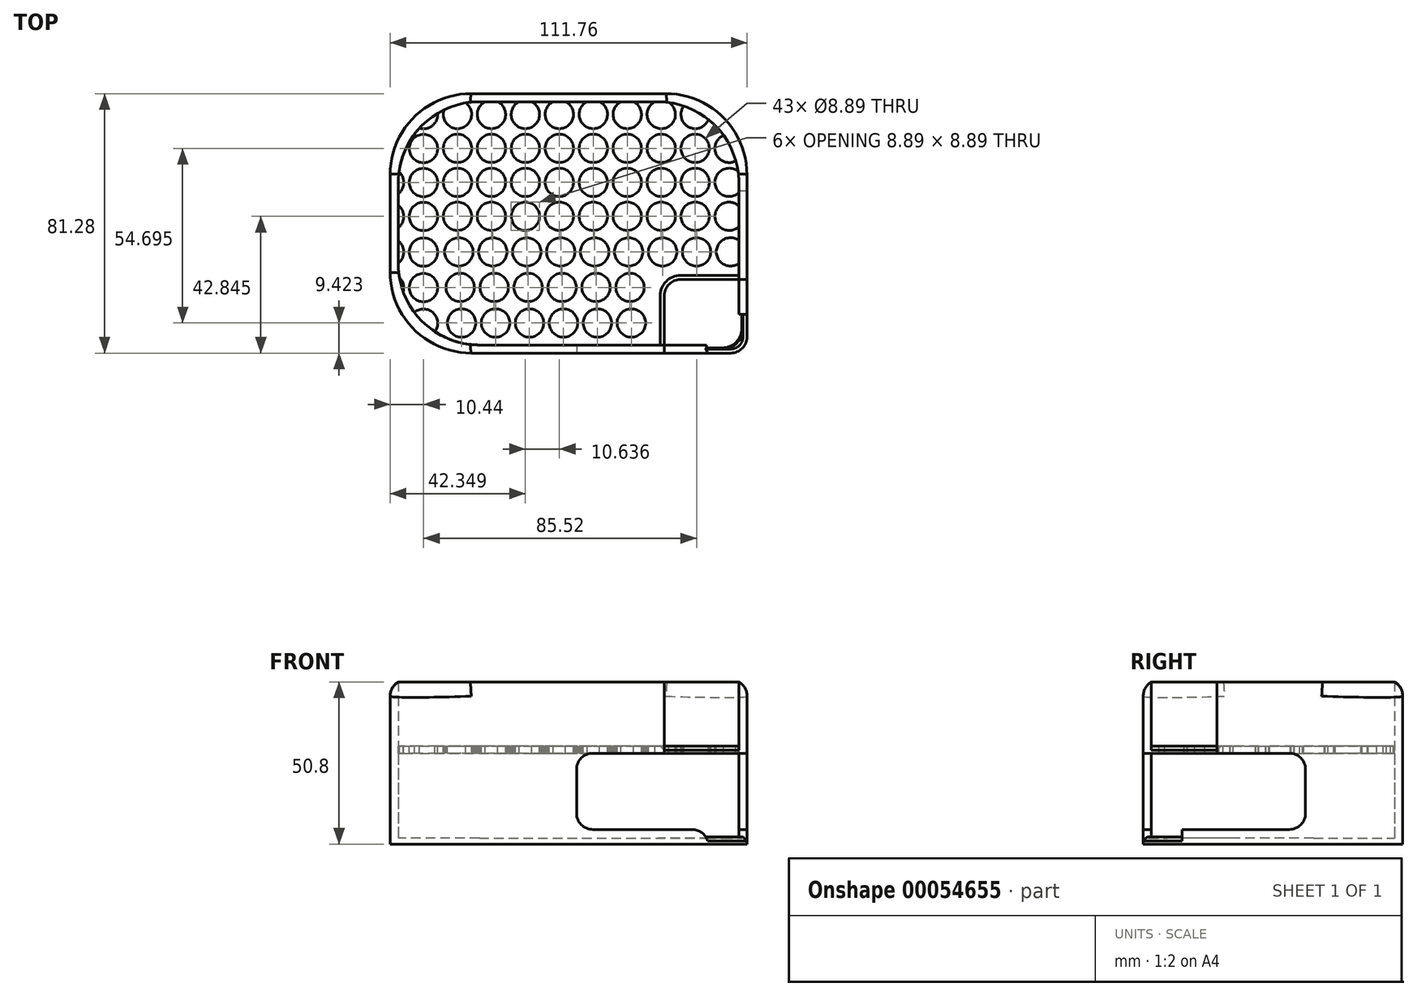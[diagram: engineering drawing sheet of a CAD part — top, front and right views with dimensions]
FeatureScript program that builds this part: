
annotation { "Feature Type Name" : "Feature", "Feature Type Description" : "" }
export const myFeature = defineFeature(function(context is Context, id is Id, definition is map)
    precondition{}
    {
        {
            var Q0;
            Q0=qCreatedBy(makeId("Top.planeOp"),FACE);
            var sketch = newSketch(context, id + "F0", { "sketchPlane" : qUnion([Q0])});
            skLineSegment(sketch, "E0.bottom", {"start": v(-52.81, 43.14) * mm, "end": v(53.87, 43.14) * mm});
            skLineSegment(sketch, "E0.top", {"start": v(-52.81, -33.06) * mm, "end": v(53.87, -33.06) * mm});
            skLineSegment(sketch, "E0.left", {"start": v(-52.81, 43.14) * mm, "end": v(-52.81, -33.06) * mm});
            skLineSegment(sketch, "E0.right", {"start": v(53.87, 43.14) * mm, "end": v(53.87, -33.06) * mm});
            skPoint(sketch, "E0.middle", {"position": v(0.53, 5.04) * mm});
            skLineSegment(sketch, "E1.bottom", {"start": v(56.4, 45.68) * mm, "end": v(-55.35, 45.68) * mm});
            skLineSegment(sketch, "E1.top", {"start": v(56.4, -35.6) * mm, "end": v(-55.35, -35.6) * mm});
            skLineSegment(sketch, "E1.left", {"start": v(56.4, 45.68) * mm, "end": v(56.4, -35.6) * mm});
            skLineSegment(sketch, "E1.right", {"start": v(-55.35, 45.68) * mm, "end": v(-55.35, -35.6) * mm});
            skSolve(sketch);
        }
        {
            var Q0;
            Q0=makeQuery(id+"F0.imprint","IMPRINT",FACE,{"disambiguationData":[TD([[makeQuery(id+"F0.imprint","IMPRINT",EDGE,{"derivedFrom":sQuery(id+"F0.wireOp",EDGE,"E0.bottom")}),-1.0]])]});
            extrude(context, id + "F1", {"entities" : qUnion([Q0]), "depth" : 1.9 * mm});
        }
        {
            var Q0;
            Q0=makeQuery(id+"F0.imprint","IMPRINT",FACE,{"disambiguationData":[TD([[makeQuery(id+"F0.imprint","IMPRINT",EDGE,{"derivedFrom":sQuery(id+"F0.wireOp",EDGE,"E0.bottom")}),1.0]])]});
            extrude(context, id + "F2", {"entities" : qUnion([Q0]), "operationType" : NewBodyOperationType.ADD, "depth" : 50.8 * mm});
        }
        {
            var Q0;
            Q0=makeQuery(id+"F2.opExtrude","SWEPT_FACE",FACE,{"disambiguationData":[OSD([sQuery(id+"F0.wireOp",EDGE,"E0.bottom")])]});
            var sketch = newSketch(context, id + "F3", { "sketchPlane" : qUnion([Q0])});
            skLineSegment(sketch, "E2.bottom", {"start": v(-52.81, 30.73) * mm, "end": v(53.87, 30.73) * mm});
            skLineSegment(sketch, "E2.top", {"start": v(-52.81, 28.45) * mm, "end": v(53.87, 28.45) * mm});
            skLineSegment(sketch, "E2.left", {"start": v(-52.81, 30.73) * mm, "end": v(-52.81, 28.45) * mm});
            skLineSegment(sketch, "E2.right", {"start": v(53.87, 30.73) * mm, "end": v(53.87, 28.45) * mm});
            skSolve(sketch);
        }
        {
            var Q0;
            Q0=makeQuery(id+"F3.imprint","IMPRINT",FACE,{"disambiguationData":[TD([[makeQuery(id+"F3.imprint","IMPRINT",EDGE,{"derivedFrom":sQuery(id+"F3.wireOp",EDGE,"E2.bottom")}),-1.0]])]});
            extrude(context, id + "F4", {"entities" : qUnion([Q0]), "operationType" : NewBodyOperationType.ADD, "depth" : 77.97 * mm});
        }
        {
            var Q0;
            Q0=makeQuery(id+"F2.opExtrude","SWEPT_FACE",FACE,{"disambiguationData":[OSD([sQuery(id+"F0.wireOp",EDGE,"E1.top")])]});
            var sketch = newSketch(context, id + "F5", { "sketchPlane" : qUnion([Q0])});
            skLineSegment(sketch, "E3.bottom", {"start": v(30.51, 50.8) * mm, "end": v(56.4, 50.8) * mm});
            skLineSegment(sketch, "E3.top", {"start": v(30.51, 4.57) * mm, "end": v(56.4, 4.57) * mm});
            skLineSegment(sketch, "E3.left", {"start": v(30.51, 50.8) * mm, "end": v(30.51, 4.57) * mm});
            skLineSegment(sketch, "E3.right", {"start": v(56.4, 50.8) * mm, "end": v(56.4, 4.57) * mm});
            skSolve(sketch);
        }
        {
            var Q0;
            Q0 = qSketchRegion(id + "F5", true);
            extrude(context, id + "F6", {"entities" : qUnion([Q0]), "operationType" : NewBodyOperationType.REMOVE, "oppositeDirection" : true, "depth" : 23.07 * mm});
        }
        {
            var Q0;
            Q0=makeQuery(id+"F2.opExtrude","SWEPT_FACE",FACE,{"disambiguationData":[OSD([sQuery(id+"F0.wireOp",EDGE,"E1.top")])]});
            var sketch = newSketch(context, id + "F7", { "sketchPlane" : qUnion([Q0])});
            skLineSegment(sketch, "E4.bottom", {"start": v(43.46, 4.57) * mm, "end": v(56.4, 4.57) * mm});
            skLineSegment(sketch, "E4.top", {"start": v(43.46, 2.29) * mm, "end": v(56.4, 2.29) * mm});
            skLineSegment(sketch, "E4.left", {"start": v(43.46, 4.57) * mm, "end": v(43.46, 2.29) * mm});
            skLineSegment(sketch, "E4.right", {"start": v(56.4, 4.57) * mm, "end": v(56.4, 2.29) * mm});
            skSolve(sketch);
        }
        {
            var Q0;
            Q0 = qSketchRegion(id + "F7", true);
            extrude(context, id + "F8", {"entities" : qUnion([Q0]), "operationType" : NewBodyOperationType.REMOVE, "oppositeDirection" : true, "depth" : 12.1 * mm});
        }
        {
            var Q0;
            {var subQ0=sQuery(id+"F0.wireOp",EDGE,"E0.bottom");var subQ1=sQuery(id+"F0.wireOp",EDGE,"E0.left");Q0=makeQuery(id+"F4.boolean.opBoolean","SPLIT",EDGE,{"disambiguationData":[TD([makeQuery(id+"F4.opExtrude","SWEPT_FACE",FACE,{"disambiguationData":[OSD([sQuery(id+"F3.wireOp",EDGE,"E2.bottom")])]})])],"derivedFrom":makeQuery(id+"F2.opExtrude","SWEPT_EDGE",EDGE,{"disambiguationData":[OSD([subQ0,subQ1])]})});}
            var Q1;
            {var subQ0=sQuery(id+"F0.wireOp",EDGE,"E0.left");var subQ1=sQuery(id+"F0.wireOp",EDGE,"E0.top");Q1=makeQuery(id+"F4.boolean.opBoolean","SPLIT",EDGE,{"disambiguationData":[TD([makeQuery(id+"F4.opExtrude","SWEPT_FACE",FACE,{"disambiguationData":[OSD([sQuery(id+"F3.wireOp",EDGE,"E2.bottom")])]})])],"derivedFrom":makeQuery(id+"F2.opExtrude","SWEPT_EDGE",EDGE,{"disambiguationData":[OSD([subQ1,subQ0])]})});}
            var Q2;
            {var subQ0=sQuery(id+"F0.wireOp",EDGE,"E0.left");var subQ1=sQuery(id+"F0.wireOp",EDGE,"E0.bottom");Q2=makeQuery(id+"F4.boolean.opBoolean","SPLIT",EDGE,{"disambiguationData":[TD([makeQuery(id+"F4.opExtrude","SWEPT_FACE",FACE,{"disambiguationData":[OSD([sQuery(id+"F3.wireOp",EDGE,"E2.top")])]})])],"derivedFrom":makeQuery(id+"F2.opExtrude","SWEPT_EDGE",EDGE,{"disambiguationData":[OSD([subQ1,subQ0])]})});}
            var Q3;
            {var subQ0=sQuery(id+"F0.wireOp",EDGE,"E0.right");var subQ1=sQuery(id+"F0.wireOp",EDGE,"E0.bottom");Q3=makeQuery(id+"F4.boolean.opBoolean","SPLIT",EDGE,{"disambiguationData":[TD([makeQuery(id+"F4.opExtrude","SWEPT_FACE",FACE,{"disambiguationData":[OSD([sQuery(id+"F3.wireOp",EDGE,"E2.top")])]})])],"derivedFrom":makeQuery(id+"F2.opExtrude","SWEPT_EDGE",EDGE,{"disambiguationData":[OSD([subQ1,subQ0])]})});}
            var Q4;
            {var subQ0=sQuery(id+"F0.wireOp",EDGE,"E0.left");var subQ1=sQuery(id+"F0.wireOp",EDGE,"E0.top");Q4=makeQuery(id+"F4.boolean.opBoolean","SPLIT",EDGE,{"disambiguationData":[TD([makeQuery(id+"F4.opExtrude","SWEPT_FACE",FACE,{"disambiguationData":[OSD([sQuery(id+"F3.wireOp",EDGE,"E2.top")])]})])],"derivedFrom":makeQuery(id+"F2.opExtrude","SWEPT_EDGE",EDGE,{"disambiguationData":[OSD([subQ1,subQ0])]})});}
            var Q5;
            {var subQ0=sQuery(id+"F0.wireOp",EDGE,"E0.bottom");var subQ1=sQuery(id+"F0.wireOp",EDGE,"E0.right");Q5=makeQuery(id+"F4.boolean.opBoolean","SPLIT",EDGE,{"disambiguationData":[TD([makeQuery(id+"F4.opExtrude","SWEPT_FACE",FACE,{"disambiguationData":[OSD([sQuery(id+"F3.wireOp",EDGE,"E2.bottom")])]})])],"derivedFrom":makeQuery(id+"F2.opExtrude","SWEPT_EDGE",EDGE,{"disambiguationData":[OSD([subQ0,subQ1])]})});}
            var Q6;
            Q6=makeQuery(id+"F2.opExtrude","SWEPT_EDGE",EDGE,{"disambiguationData":[OSD([sQuery(id+"F0.wireOp",EDGE,"E1.bottom"),sQuery(id+"F0.wireOp",EDGE,"E1.left")])]});
            var Q7;
            Q7=makeQuery(id+"F2.opExtrude","SWEPT_EDGE",EDGE,{"disambiguationData":[OSD([sQuery(id+"F0.wireOp",EDGE,"E1.bottom"),sQuery(id+"F0.wireOp",EDGE,"E1.right")])]});
            var Q8;
            Q8=makeQuery(id+"F2.opExtrude","SWEPT_EDGE",EDGE,{"disambiguationData":[OSD([sQuery(id+"F0.wireOp",EDGE,"E1.top"),sQuery(id+"F0.wireOp",EDGE,"E1.right")])]});
            fillet(context, id + "F9", {"entities" : qUnion([Q0, Q1, Q2, Q3, Q4, Q5, Q6, Q7, Q8]), "radius" : 25.4 * mm, "tangentPropagation" : true, "allowEdgeOverflow" : false});
        }
        {
            var Q0;
            Q0=makeQuery(id+"F6.boolean.opBoolean","COPY",FACE,{"derivedFrom":makeQuery(id+"F6.opExtrude","SWEPT_FACE",FACE,{"disambiguationData":[OSD([sQuery(id+"F5.wireOp",EDGE,"E3.left")])]})});
            var sketch = newSketch(context, id + "F10", { "sketchPlane" : qUnion([Q0])});
            skLineSegment(sketch, "E5.bottom", {"start": v(-33.06, 28.45) * mm, "end": v(-35.6, 28.45) * mm});
            skLineSegment(sketch, "E5.top", {"start": v(-33.06, 4.57) * mm, "end": v(-35.6, 4.57) * mm});
            skLineSegment(sketch, "E5.left", {"start": v(-33.06, 28.45) * mm, "end": v(-33.06, 4.57) * mm});
            skLineSegment(sketch, "E5.right", {"start": v(-35.6, 28.45) * mm, "end": v(-35.6, 4.57) * mm});
            skSolve(sketch);
        }
        {
            var Q0;
            Q0 = qSketchRegion(id + "F10", true);
            extrude(context, id + "F11", {"entities" : qUnion([Q0]), "operationType" : NewBodyOperationType.REMOVE, "oppositeDirection" : true, "depth" : 27.48 * mm});
        }
        {
            var Q0;
            Q0=makeQuery(id+"F6.boolean.opBoolean","COPY",FACE,{"derivedFrom":makeQuery(id+"F6.opExtrude","CAP_FACE",FACE,{"disambiguationData":[OSD([sQuery(id+"F5.wireOp",EDGE,"E3.bottom"),sQuery(id+"F5.wireOp",EDGE,"E3.top"),sQuery(id+"F5.wireOp",EDGE,"E3.left"),sQuery(id+"F5.wireOp",EDGE,"E3.right")])],"isStart":false})});
            var sketch = newSketch(context, id + "F12", { "sketchPlane" : qUnion([Q0])});
            skLineSegment(sketch, "E6.bottom", {"start": v(53.87, 28.45) * mm, "end": v(56.4, 28.45) * mm});
            skLineSegment(sketch, "E6.top", {"start": v(53.87, 4.57) * mm, "end": v(56.4, 4.57) * mm});
            skLineSegment(sketch, "E6.left", {"start": v(53.87, 28.45) * mm, "end": v(53.87, 4.57) * mm});
            skLineSegment(sketch, "E6.right", {"start": v(56.4, 28.45) * mm, "end": v(56.4, 4.57) * mm});
            skSolve(sketch);
        }
        {
            var Q0;
            Q0 = qSketchRegion(id + "F12", true);
            extrude(context, id + "F13", {"entities" : qUnion([Q0]), "operationType" : NewBodyOperationType.REMOVE, "oppositeDirection" : true, "depth" : 27.75 * mm});
        }
        {
            var Q0;
            Q0=makeQuery(id+"F6.boolean.opBoolean","COPY",EDGE,{"derivedFrom":makeQuery(id+"F6.opExtrude","CAP_EDGE",EDGE,{"disambiguationData":[OSD([sQuery(id+"F5.wireOp",EDGE,"E3.left")])],"isStart":false})});
            var Q1;
            Q1=makeQuery(id+"F13.boolean.opBoolean","COPY",EDGE,{"derivedFrom":makeQuery(id+"F13.opExtrude","CAP_EDGE",EDGE,{"disambiguationData":[OSD([sQuery(id+"F12.wireOp",EDGE,"E6.bottom")])],"isStart":false})});
            var Q2;
            Q2=makeQuery(id+"F13.boolean.opBoolean","COPY",EDGE,{"derivedFrom":makeQuery(id+"F13.opExtrude","CAP_EDGE",EDGE,{"disambiguationData":[OSD([sQuery(id+"F12.wireOp",EDGE,"E6.top")])],"isStart":false})});
            var Q3;
            Q3=makeQuery(id+"F8.boolean.opBoolean","COPY",EDGE,{"derivedFrom":makeQuery(id+"F8.opExtrude","CAP_EDGE",EDGE,{"disambiguationData":[OSD([sQuery(id+"F7.wireOp",EDGE,"E4.bottom")])],"isStart":false})});
            var Q4;
            Q4=makeQuery(id+"F8.boolean.opBoolean","COPY",EDGE,{"derivedFrom":makeQuery(id+"F8.opExtrude","SWEPT_EDGE",EDGE,{"disambiguationData":[OSD([sQuery(id+"F5.wireOp",EDGE,"E3.top"),sQuery(id+"F7.wireOp",EDGE,"E4.bottom"),sQuery(id+"F7.wireOp",EDGE,"E4.left")])]})});
            var Q5;
            Q5=makeQuery(id+"F2.opExtrude","SWEPT_EDGE",EDGE,{"disambiguationData":[OSD([sQuery(id+"F0.wireOp",EDGE,"E1.top"),sQuery(id+"F0.wireOp",EDGE,"E1.left")])]});
            var Q6;
            Q6=makeQuery(id+"F11.boolean.opBoolean","COPY",EDGE,{"derivedFrom":makeQuery(id+"F11.opExtrude","CAP_EDGE",EDGE,{"disambiguationData":[OSD([sQuery(id+"F10.wireOp",EDGE,"E5.top")])],"isStart":false})});
            var Q7;
            Q7=makeQuery(id+"F11.boolean.opBoolean","COPY",EDGE,{"derivedFrom":makeQuery(id+"F11.opExtrude","CAP_EDGE",EDGE,{"disambiguationData":[OSD([sQuery(id+"F10.wireOp",EDGE,"E5.bottom")])],"isStart":false})});
            var Q8;
            Q8=makeQuery(id+"F6.boolean.opBoolean","COPY",EDGE,{"derivedFrom":makeQuery(id+"F6.opExtrude","CAP_EDGE",EDGE,{"disambiguationData":[OSD([sQuery(id+"F5.wireOp",EDGE,"E3.left")])],"isStart":true})});
            var Q9;
            Q9=makeQuery(id+"F6.boolean.opBoolean","COPY",EDGE,{"derivedFrom":makeQuery(id+"F6.opExtrude","CAP_EDGE",EDGE,{"disambiguationData":[OSD([sQuery(id+"F5.wireOp",EDGE,"E3.right")])],"isStart":false})});
            var Q10;
            Q10=makeQuery(id+"F2.opExtrude","CAP_EDGE",EDGE,{"disambiguationData":[OSD([sQuery(id+"F0.wireOp",EDGE,"E1.left")])],"isStart":false});
            fillet(context, id + "F14", {"entities" : qUnion([Q0, Q1, Q2, Q3, Q4, Q5, Q6, Q7, Q8, Q9, Q10]), "radius" : 5.08 * mm, "tangentPropagation" : true, "allowEdgeOverflow" : false});
        }
        {
            var Q0;
            {var subQ0=sQuery(id+"F0.wireOp",EDGE,"E0.right");var subQ1=sQuery(id+"F0.wireOp",EDGE,"E0.top");Q0=makeQuery(id+"F4.boolean.opBoolean","SPLIT",EDGE,{"disambiguationData":[TD([makeQuery(id+"F4.opExtrude","SWEPT_FACE",FACE,{"disambiguationData":[OSD([sQuery(id+"F3.wireOp",EDGE,"E2.top")])]})])],"derivedFrom":makeQuery(id+"F2.opExtrude","SWEPT_EDGE",EDGE,{"disambiguationData":[OSD([subQ1,subQ0])]})});}
            fillet(context, id + "F15", {"entities" : qUnion([Q0]), "radius" : 5.08 * mm, "tangentPropagation" : true, "allowEdgeOverflow" : false});
        }
        {
            var Q0;
            Q0=makeQuery(id+"F14.opFillet","BLEND_EDGE",EDGE,{"blendedFrom":[makeQuery(id+"F2.opExtrude","SWEPT_EDGE",EDGE,{"disambiguationData":[OSD([sQuery(id+"F0.wireOp",EDGE,"E1.top"),sQuery(id+"F0.wireOp",EDGE,"E1.left")])]}),makeQuery(id+"F8.boolean.opBoolean","COPY",FACE,{"derivedFrom":makeQuery(id+"F8.opExtrude","SWEPT_FACE",FACE,{"disambiguationData":[OSD([sQuery(id+"F7.wireOp",EDGE,"E4.top")])]})})],"blendedInto":[makeQuery(id+"F8.boolean.opBoolean","COPY",FACE,{"derivedFrom":makeQuery(id+"F8.opExtrude","SWEPT_FACE",FACE,{"disambiguationData":[OSD([sQuery(id+"F7.wireOp",EDGE,"E4.top")])]})})]});
            var Q1;
            {var subQ0=sQuery(id+"F0.wireOp",EDGE,"E0.right");var subQ1=sQuery(id+"F0.wireOp",EDGE,"E0.top");Q1=makeQuery(id+"F15.opFillet","BLEND_EDGE",EDGE,{"blendedFrom":[makeQuery(id+"F4.boolean.opBoolean","SPLIT",EDGE,{"disambiguationData":[TD([makeQuery(id+"F4.opExtrude","SWEPT_FACE",FACE,{"disambiguationData":[OSD([sQuery(id+"F3.wireOp",EDGE,"E2.top")])]})])],"derivedFrom":makeQuery(id+"F2.opExtrude","SWEPT_EDGE",EDGE,{"disambiguationData":[OSD([subQ1,subQ0])]})}),makeQuery(id+"F8.boolean.opBoolean","COPY",FACE,{"derivedFrom":makeQuery(id+"F8.opExtrude","SWEPT_FACE",FACE,{"disambiguationData":[OSD([sQuery(id+"F7.wireOp",EDGE,"E4.top")])]})})],"blendedInto":[makeQuery(id+"F8.boolean.opBoolean","COPY",FACE,{"derivedFrom":makeQuery(id+"F8.opExtrude","SWEPT_FACE",FACE,{"disambiguationData":[OSD([sQuery(id+"F7.wireOp",EDGE,"E4.top")])]})})]});}
            var Q2;
            Q2=makeQuery(id+"F14.opFillet","BLEND_EDGE",EDGE,{"blendedFrom":[makeQuery(id+"F6.boolean.opBoolean","COPY",EDGE,{"derivedFrom":makeQuery(id+"F6.opExtrude","CAP_EDGE",EDGE,{"disambiguationData":[OSD([sQuery(id+"F5.wireOp",EDGE,"E3.left")])],"isStart":false})}),makeQuery(id+"F4.opExtrude","SWEPT_FACE",FACE,{"disambiguationData":[OSD([sQuery(id+"F3.wireOp",EDGE,"E2.bottom")])]})],"blendedInto":[makeQuery(id+"F4.opExtrude","SWEPT_FACE",FACE,{"disambiguationData":[OSD([sQuery(id+"F3.wireOp",EDGE,"E2.bottom")])]})]});
            var Q3;
            Q3=makeQuery(id+"F11.boolean.opBoolean","COPY",EDGE,{"derivedFrom":makeQuery(id+"F11.opExtrude","CAP_EDGE",EDGE,{"disambiguationData":[OSD([sQuery(id+"F10.wireOp",EDGE,"E5.right")])],"isStart":false})});
            chamfer(context, id + "F16", {"entities" : qUnion([Q0, Q1, Q2, Q3]), "width" : 1.27 * mm, "tangentPropagation" : true});
        }
        {
            var Q0;
            Q0=makeQuery(id+"F4.opExtrude","SWEPT_FACE",FACE,{"disambiguationData":[OSD([sQuery(id+"F3.wireOp",EDGE,"E2.bottom")])]});
            var sketch = newSketch(context, id + "F17", { "sketchPlane" : qUnion([Q0])});
            skCircle(sketch, "E7", {"center": v(-34.27, 7.25) * mm, "radius": 4.44 * mm});
            skCircle(sketch, "E8.0.1.0", {"center": v(-34.27, 17.88) * mm, "radius": 4.44 * mm});
            skCircle(sketch, "E8.0.2.0", {"center": v(-34.27, 28.52) * mm, "radius": 4.44 * mm});
            skArc(sketch, "E8.0.3.0", {"start": v(-38.47, 40.61) * mm, "mid": v(-32.92, 34.92) * mm, "end": v(-31.7, 42.78) * mm});
            skCircle(sketch, "E8.1.0.0", {"center": v(-23.64, 7.25) * mm, "radius": 4.44 * mm});
            skCircle(sketch, "E8.1.1.0", {"center": v(-23.64, 17.88) * mm, "radius": 4.44 * mm});
            skCircle(sketch, "E8.1.2.0", {"center": v(-23.64, 28.52) * mm, "radius": 4.44 * mm});
            skArc(sketch, "E8.1.3.0", {"start": v(-25.6, 43.14) * mm, "mid": v(-23.64, 34.71) * mm, "end": v(-21.68, 43.14) * mm});
            skCircle(sketch, "E8.2.0.0", {"center": v(-13, 7.25) * mm, "radius": 4.44 * mm});
            skCircle(sketch, "E8.2.1.0", {"center": v(-13, 17.88) * mm, "radius": 4.44 * mm});
            skCircle(sketch, "E8.2.2.0", {"center": v(-13, 28.52) * mm, "radius": 4.44 * mm});
            skArc(sketch, "E8.2.3.0", {"start": v(-14.96, 43.14) * mm, "mid": v(-13, 34.71) * mm, "end": v(-11.05, 43.14) * mm});
            skCircle(sketch, "E8.3.0.0", {"center": v(-2.37, 7.25) * mm, "radius": 4.44 * mm});
            skCircle(sketch, "E8.3.1.0", {"center": v(-2.37, 17.88) * mm, "radius": 4.44 * mm});
            skCircle(sketch, "E8.3.2.0", {"center": v(-2.37, 28.52) * mm, "radius": 4.44 * mm});
            skArc(sketch, "E8.3.3.0", {"start": v(-4.32, 43.14) * mm, "mid": v(-2.37, 34.71) * mm, "end": v(-0.4, 43.14) * mm});
            skCircle(sketch, "E8.4.0.0", {"center": v(8.27, 7.25) * mm, "radius": 4.44 * mm});
            skCircle(sketch, "E8.4.1.0", {"center": v(8.27, 17.88) * mm, "radius": 4.44 * mm});
            skCircle(sketch, "E8.4.2.0", {"center": v(8.27, 28.52) * mm, "radius": 4.44 * mm});
            skArc(sketch, "E8.4.3.0", {"start": v(6.32, 43.14) * mm, "mid": v(8.27, 34.71) * mm, "end": v(10.23, 43.14) * mm});
            skCircle(sketch, "E8.5.0.0", {"center": v(18.9, 7.25) * mm, "radius": 4.44 * mm});
            skCircle(sketch, "E8.5.1.0", {"center": v(18.9, 17.88) * mm, "radius": 4.44 * mm});
            skCircle(sketch, "E8.5.2.0", {"center": v(18.9, 28.52) * mm, "radius": 4.44 * mm});
            skArc(sketch, "E8.5.3.0", {"start": v(16.95, 43.14) * mm, "mid": v(18.9, 34.71) * mm, "end": v(20.86, 43.14) * mm});
            skCircle(sketch, "E8.6.0.0", {"center": v(29.54, 7.25) * mm, "radius": 4.44 * mm});
            skCircle(sketch, "E8.6.1.0", {"center": v(29.54, 17.88) * mm, "radius": 4.44 * mm});
            skCircle(sketch, "E8.6.2.0", {"center": v(29.54, 28.52) * mm, "radius": 4.44 * mm});
            skArc(sketch, "E8.6.3.0", {"start": v(27.59, 43.14) * mm, "mid": v(29.3, 34.72) * mm, "end": v(31.92, 42.9) * mm});
            skCircle(sketch, "E8.7.0.0", {"center": v(40.18, 7.25) * mm, "radius": 4.44 * mm});
            skCircle(sketch, "E8.7.1.0", {"center": v(40.18, 17.88) * mm, "radius": 4.44 * mm});
            skCircle(sketch, "E8.7.2.0", {"center": v(40.18, 28.52) * mm, "radius": 4.44 * mm});
            skArc(sketch, "E8.7.3.0", {"start": v(36.61, 41.8) * mm, "mid": v(38.05, 35.26) * mm, "end": v(44.33, 37.58) * mm});
            skArc(sketch, "E8.8.0.0", {"start": v(53.87, 10.48) * mm, "mid": v(46.37, 7.25) * mm, "end": v(53.87, 4.01) * mm});
            skArc(sketch, "E8.8.1.0", {"start": v(53.6, 21.34) * mm, "mid": v(46.38, 17.71) * mm, "end": v(53.87, 14.65) * mm});
            skArc(sketch, "E8.8.2.0", {"start": v(49.07, 32.6) * mm, "mid": v(46.81, 26.59) * mm, "end": v(52.92, 24.6) * mm});
            skLineSegment(sketch, "E8.direction1", {"start": v(-34.27, 7.25) * mm, "end": v(-23.64, 7.25) * mm, "construction": true});
            skLineSegment(sketch, "E8.direction2", {"start": v(-34.27, 7.25) * mm, "end": v(-34.27, 17.88) * mm, "construction": true});
            skPoint(sketch, "E9", {"position": v(-38.47, 40.61) * mm});
            skPoint(sketch, "E10", {"position": v(-31.7, 42.78) * mm});
            skPoint(sketch, "E11", {"position": v(-21.68, 43.14) * mm});
            skPoint(sketch, "E12", {"position": v(-11.05, 43.14) * mm});
            skPoint(sketch, "E13", {"position": v(-14.96, 43.14) * mm});
            skPoint(sketch, "E14", {"position": v(-4.32, 43.14) * mm});
            skPoint(sketch, "E15", {"position": v(-0.4, 43.14) * mm});
            skPoint(sketch, "E16", {"position": v(16.95, 43.14) * mm});
            skPoint(sketch, "E17", {"position": v(20.86, 43.14) * mm});
            skPoint(sketch, "E18", {"position": v(10.23, 43.14) * mm});
            skPoint(sketch, "E19", {"position": v(6.32, 43.14) * mm});
            skPoint(sketch, "E20", {"position": v(-25.6, 43.14) * mm});
            skPoint(sketch, "E21", {"position": v(27.59, 43.14) * mm});
            skPoint(sketch, "E22", {"position": v(31.92, 42.9) * mm});
            skPoint(sketch, "E23", {"position": v(36.61, 41.8) * mm});
            skPoint(sketch, "E24", {"position": v(44.33, 37.58) * mm});
            skPoint(sketch, "E25", {"position": v(49.07, 32.6) * mm});
            skPoint(sketch, "E26", {"position": v(52.92, 24.6) * mm});
            skPoint(sketch, "E27", {"position": v(53.6, 21.34) * mm});
            skPoint(sketch, "E28", {"position": v(53.87, 14.65) * mm});
            skPoint(sketch, "E29", {"position": v(53.87, 10.48) * mm});
            skPoint(sketch, "E30", {"position": v(53.87, 4.01) * mm});
            skCircle(sketch, "E31.0.1.0", {"center": v(-33.84, -3.9) * mm, "radius": 4.44 * mm});
            skCircle(sketch, "E31.0.2.0", {"center": v(-33.41, -15.04) * mm, "radius": 4.44 * mm});
            skCircle(sketch, "E31.0.3.0", {"center": v(-32.99, -26.18) * mm, "radius": 4.44 * mm});
            skCircle(sketch, "E31.1.1.0", {"center": v(-23.2, -3.9) * mm, "radius": 4.44 * mm});
            skCircle(sketch, "E31.1.2.0", {"center": v(-22.78, -15.04) * mm, "radius": 4.44 * mm});
            skCircle(sketch, "E31.1.3.0", {"center": v(-22.35, -26.18) * mm, "radius": 4.44 * mm});
            skCircle(sketch, "E31.2.1.0", {"center": v(-12.57, -3.9) * mm, "radius": 4.44 * mm});
            skCircle(sketch, "E31.2.2.0", {"center": v(-12.14, -15.04) * mm, "radius": 4.44 * mm});
            skCircle(sketch, "E31.2.3.0", {"center": v(-11.71, -26.18) * mm, "radius": 4.44 * mm});
            skCircle(sketch, "E31.3.1.0", {"center": v(-1.94, -3.9) * mm, "radius": 4.44 * mm});
            skCircle(sketch, "E31.3.2.0", {"center": v(-1.5, -15.04) * mm, "radius": 4.44 * mm});
            skCircle(sketch, "E31.3.3.0", {"center": v(-1.08, -26.18) * mm, "radius": 4.44 * mm});
            skCircle(sketch, "E31.4.1.0", {"center": v(8.7, -3.9) * mm, "radius": 4.44 * mm});
            skCircle(sketch, "E31.4.2.0", {"center": v(9.13, -15.04) * mm, "radius": 4.44 * mm});
            skCircle(sketch, "E31.4.3.0", {"center": v(9.56, -26.18) * mm, "radius": 4.44 * mm});
            skCircle(sketch, "E31.5.1.0", {"center": v(19.34, -3.9) * mm, "radius": 4.44 * mm});
            skCircle(sketch, "E31.5.2.0", {"center": v(19.77, -15.04) * mm, "radius": 4.44 * mm});
            skCircle(sketch, "E31.5.3.0", {"center": v(20.2, -26.18) * mm, "radius": 4.44 * mm});
            skCircle(sketch, "E31.6.1.0", {"center": v(29.97, -3.9) * mm, "radius": 4.44 * mm});
            skCircle(sketch, "E31.7.1.0", {"center": v(40.6, -3.9) * mm, "radius": 4.44 * mm});
            skArc(sketch, "E31.8.0.0", {"start": v(50.82, 11.69) * mm, "mid": v(46.37, 7.25) * mm, "end": v(50.82, 2.8) * mm});
            skArc(sketch, "E31.8.1.0", {"start": v(53.87, -0.3) * mm, "mid": v(46.8, -3.9) * mm, "end": v(53.87, -7.48) * mm});
            skLineSegment(sketch, "E31.direction2", {"start": v(-34.27, 7.25) * mm, "end": v(-33.84, -3.9) * mm, "construction": true});
            skPoint(sketch, "E32", {"position": v(53.87, -0.3) * mm});
            skPoint(sketch, "E33", {"position": v(53.87, -7.48) * mm});
            skCircle(sketch, "E34", {"center": v(-44.91, 7.2) * mm, "radius": 4.44 * mm});
            skCircle(sketch, "E35.0.1.0", {"center": v(-44.91, 17.83) * mm, "radius": 4.44 * mm});
            skCircle(sketch, "E35.0.2.0", {"center": v(-44.91, 28.46) * mm, "radius": 4.44 * mm});
            skArc(sketch, "E35.0.3.0", {"start": v(-46.2, 34.85) * mm, "mid": v(-42.1, 35.66) * mm, "end": v(-40.49, 39.52) * mm});
            skArc(sketch, "E35.1.0.0", {"start": v(-52.81, 3.69) * mm, "mid": v(-51.1, 7.2) * mm, "end": v(-52.81, 10.7) * mm});
            skArc(sketch, "E35.1.1.0", {"start": v(-52.81, 14.32) * mm, "mid": v(-51.1, 17.68) * mm, "end": v(-52.59, 21.14) * mm});
            skLineSegment(sketch, "E35.direction1", {"start": v(-44.91, 7.2) * mm, "end": v(-55.55, 7.2) * mm, "construction": true});
            skLineSegment(sketch, "E35.direction2", {"start": v(-44.91, 7.2) * mm, "end": v(-44.91, 17.83) * mm, "construction": true});
            skPoint(sketch, "E36", {"position": v(-52.81, 3.69) * mm});
            skPoint(sketch, "E37", {"position": v(-52.81, 10.7) * mm});
            skPoint(sketch, "E38", {"position": v(-52.81, 14.32) * mm});
            skPoint(sketch, "E39", {"position": v(-52.59, 21.14) * mm});
            skPoint(sketch, "E40", {"position": v(-46.2, 34.85) * mm});
            skPoint(sketch, "E41", {"position": v(-40.49, 39.52) * mm});
            skCircle(sketch, "E42.0.1.0", {"center": v(-44.91, -3.95) * mm, "radius": 4.44 * mm});
            skCircle(sketch, "E42.0.2.0", {"center": v(-44.91, -15.1) * mm, "radius": 4.44 * mm});
            skArc(sketch, "E42.0.3.0", {"start": v(-41.35, -28.9) * mm, "mid": v(-41.86, -23) * mm, "end": v(-47.77, -22.84) * mm});
            skArc(sketch, "E42.1.1.0", {"start": v(-52.81, -7.46) * mm, "mid": v(-51.1, -3.95) * mm, "end": v(-52.81, -0.45) * mm});
            skArc(sketch, "E42.1.2.0", {"start": v(-51.28, -16.34) * mm, "mid": v(-51.25, -13.96) * mm, "end": v(-52.46, -11.9) * mm});
            skLineSegment(sketch, "E42.direction2", {"start": v(-44.91, 7.2) * mm, "end": v(-44.91, -3.95) * mm, "construction": true});
            skPoint(sketch, "E43", {"position": v(-52.81, -7.46) * mm});
            skPoint(sketch, "E44", {"position": v(-52.81, -0.45) * mm});
            skPoint(sketch, "E45", {"position": v(-52.46, -11.9) * mm});
            skPoint(sketch, "E46", {"position": v(-51.28, -16.34) * mm});
            skPoint(sketch, "E47", {"position": v(-47.77, -22.84) * mm});
            skPoint(sketch, "E48", {"position": v(-41.35, -28.9) * mm});
            skPoint(sketch, "E49", {"position": v(-70.5, -21.36) * mm});
            skSolve(sketch);
        }
        {
            var Q0;
            Q0 = qSketchRegion(id + "F17", true);
            var Q1;
            {var subQ0=sQuery(id+"F17.wireOp",EDGE,"E8.2.3.0");Q1=makeQuery(id+"F17.imprint","IMPRINT",FACE,{"disambiguationData":[TD([[makeQuery(id+"F17.imprint","IMPRINT",EDGE,{"derivedFrom":subQ0}),1.0]])]});}
            var Q2;
            {var subQ0=sQuery(id+"F17.wireOp",EDGE,"E8.1.3.0");Q2=makeQuery(id+"F17.imprint","IMPRINT",FACE,{"disambiguationData":[TD([[makeQuery(id+"F17.imprint","IMPRINT",EDGE,{"derivedFrom":subQ0}),1.0]])]});}
            var Q3;
            {var subQ0=sQuery(id+"F17.wireOp",EDGE,"E8.0.3.0");Q3=makeQuery(id+"F17.imprint","IMPRINT",FACE,{"disambiguationData":[TD([[makeQuery(id+"F17.imprint","IMPRINT",EDGE,{"derivedFrom":subQ0}),1.0]])]});}
            var Q4;
            {var subQ0=sQuery(id+"F17.wireOp",EDGE,"E35.0.3.0");Q4=makeQuery(id+"F17.imprint","IMPRINT",FACE,{"disambiguationData":[TD([[makeQuery(id+"F17.imprint","IMPRINT",EDGE,{"derivedFrom":subQ0}),1.0]])]});}
            var Q5;
            {var subQ0=sQuery(id+"F17.wireOp",EDGE,"E35.1.1.0");Q5=makeQuery(id+"F17.imprint","IMPRINT",FACE,{"disambiguationData":[TD([[makeQuery(id+"F17.imprint","IMPRINT",EDGE,{"derivedFrom":subQ0}),1.0]])]});}
            var Q6;
            {var subQ0=sQuery(id+"F17.wireOp",EDGE,"E35.1.0.0");Q6=makeQuery(id+"F17.imprint","IMPRINT",FACE,{"disambiguationData":[TD([[makeQuery(id+"F17.imprint","IMPRINT",EDGE,{"derivedFrom":subQ0}),1.0]])]});}
            var Q7;
            {var subQ0=sQuery(id+"F17.wireOp",EDGE,"E42.1.1.0");Q7=makeQuery(id+"F17.imprint","IMPRINT",FACE,{"disambiguationData":[TD([[makeQuery(id+"F17.imprint","IMPRINT",EDGE,{"derivedFrom":subQ0}),1.0]])]});}
            var Q8;
            {var subQ0=sQuery(id+"F17.wireOp",EDGE,"E42.1.2.0");Q8=makeQuery(id+"F17.imprint","IMPRINT",FACE,{"disambiguationData":[TD([[makeQuery(id+"F17.imprint","IMPRINT",EDGE,{"derivedFrom":subQ0}),1.0]])]});}
            var Q9;
            {var subQ0=sQuery(id+"F17.wireOp",EDGE,"E42.0.3.0");Q9=makeQuery(id+"F17.imprint","IMPRINT",FACE,{"disambiguationData":[TD([[makeQuery(id+"F17.imprint","IMPRINT",EDGE,{"derivedFrom":subQ0}),1.0]])]});}
            var Q10;
            {var subQ0=sQuery(id+"F17.wireOp",EDGE,"E31.8.1.0");Q10=makeQuery(id+"F17.imprint","IMPRINT",FACE,{"disambiguationData":[TD([[makeQuery(id+"F17.imprint","IMPRINT",EDGE,{"derivedFrom":subQ0}),1.0]])]});}
            var Q11;
            {var subQ0=sQuery(id+"F17.wireOp",EDGE,"E8.8.0.0");var subQ3=sQuery(id+"F17.wireOp",EDGE,"E31.8.0.0");var subQ4=makeQuery(id+"F17.imprint","INTERSECT",VERTEX,{"disambiguationData":[OD(0.0)],"derivedFrom":[subQ0,subQ3]});Q11=makeQuery(id+"F17.imprint","IMPRINT",FACE,{"disambiguationData":[TD([[makeQuery(id+"F17.imprint","IMPRINT",EDGE,{"disambiguationData":[TD([[subQ4,-1.0]])],"derivedFrom":subQ0}),1.0]])]});}
            var Q12;
            {var subQ0=sQuery(id+"F17.wireOp",EDGE,"E8.8.1.0");Q12=makeQuery(id+"F17.imprint","IMPRINT",FACE,{"disambiguationData":[TD([[makeQuery(id+"F17.imprint","IMPRINT",EDGE,{"derivedFrom":subQ0}),1.0]])]});}
            var Q13;
            {var subQ0=sQuery(id+"F17.wireOp",EDGE,"E8.8.2.0");Q13=makeQuery(id+"F17.imprint","IMPRINT",FACE,{"disambiguationData":[TD([[makeQuery(id+"F17.imprint","IMPRINT",EDGE,{"derivedFrom":subQ0}),1.0]])]});}
            var Q14;
            {var subQ0=sQuery(id+"F17.wireOp",EDGE,"E8.7.3.0");Q14=makeQuery(id+"F17.imprint","IMPRINT",FACE,{"disambiguationData":[TD([[makeQuery(id+"F17.imprint","IMPRINT",EDGE,{"derivedFrom":subQ0}),1.0]])]});}
            var Q15;
            {var subQ0=sQuery(id+"F17.wireOp",EDGE,"E8.6.3.0");Q15=makeQuery(id+"F17.imprint","IMPRINT",FACE,{"disambiguationData":[TD([[makeQuery(id+"F17.imprint","IMPRINT",EDGE,{"derivedFrom":subQ0}),1.0]])]});}
            var Q16;
            {var subQ0=sQuery(id+"F17.wireOp",EDGE,"E8.5.3.0");Q16=makeQuery(id+"F17.imprint","IMPRINT",FACE,{"disambiguationData":[TD([[makeQuery(id+"F17.imprint","IMPRINT",EDGE,{"derivedFrom":subQ0}),1.0]])]});}
            var Q17;
            {var subQ0=sQuery(id+"F17.wireOp",EDGE,"E8.4.3.0");Q17=makeQuery(id+"F17.imprint","IMPRINT",FACE,{"disambiguationData":[TD([[makeQuery(id+"F17.imprint","IMPRINT",EDGE,{"derivedFrom":subQ0}),1.0]])]});}
            var Q18;
            {var subQ0=sQuery(id+"F17.wireOp",EDGE,"E8.3.3.0");Q18=makeQuery(id+"F17.imprint","IMPRINT",FACE,{"disambiguationData":[TD([[makeQuery(id+"F17.imprint","IMPRINT",EDGE,{"derivedFrom":subQ0}),1.0]])]});}
            extrude(context, id + "F18", {"entities" : qUnion([Q0, Q1, Q2, Q3, Q4, Q5, Q6, Q7, Q8, Q9, Q10, Q11, Q12, Q13, Q14, Q15, Q16, Q17, Q18]), "operationType" : NewBodyOperationType.REMOVE, "oppositeDirection" : true, "depth" : 11.26 * mm});
        }
    });
